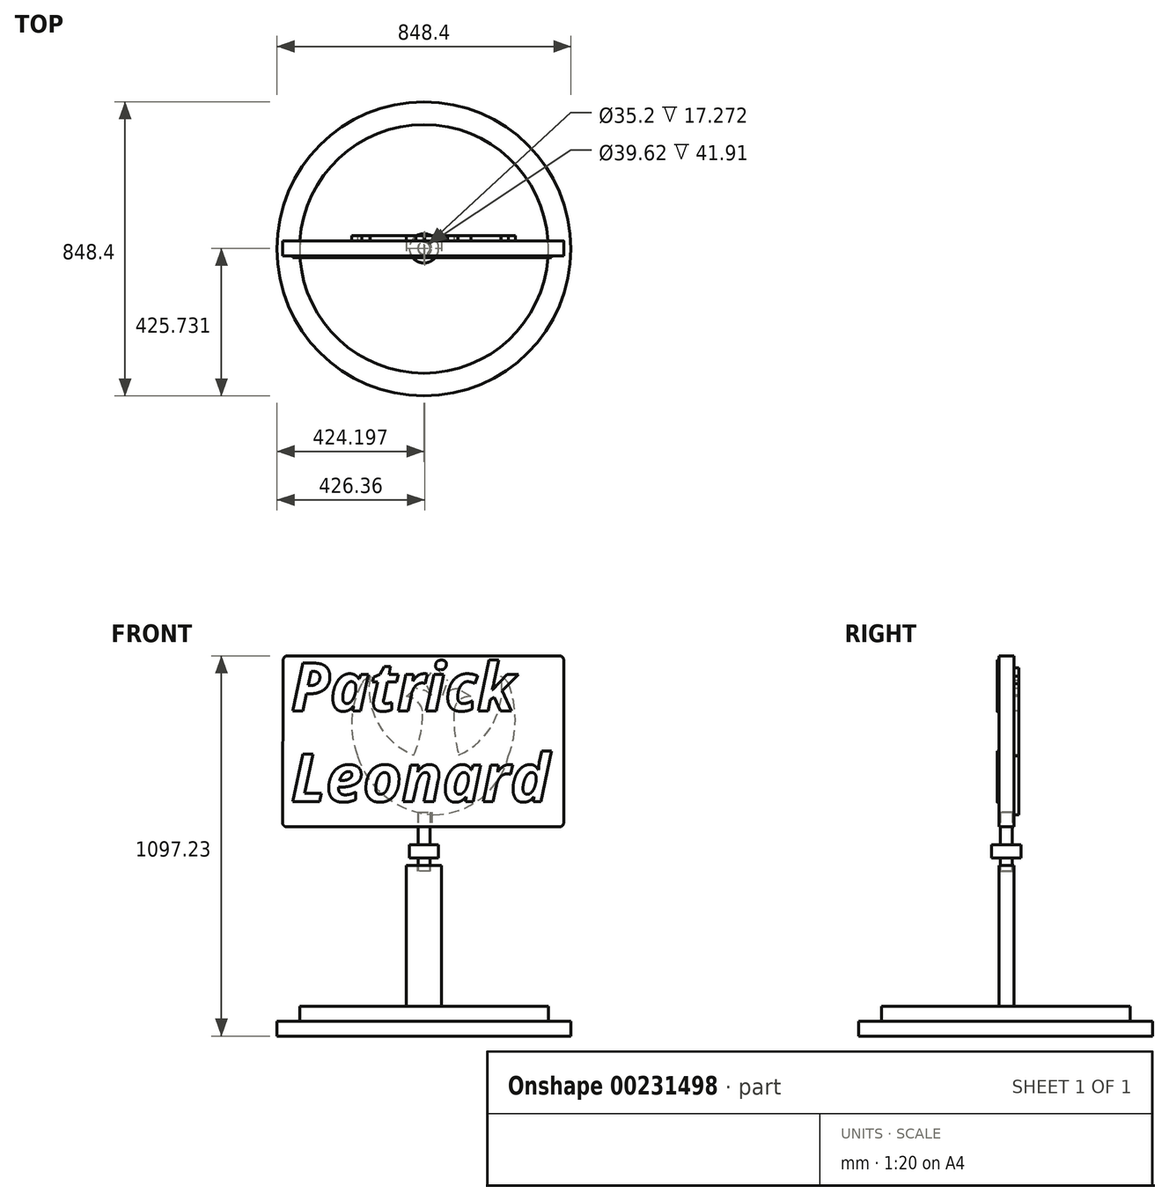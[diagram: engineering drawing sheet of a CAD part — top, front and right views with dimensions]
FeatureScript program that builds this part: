
annotation { "Feature Type Name" : "Feature", "Feature Type Description" : "" }
export const myFeature = defineFeature(function(context is Context, id is Id, definition is map)
    precondition{}
    {
        {
            var Q0;
            Q0=qCreatedBy(makeId("Front.planeOp"),FACE);
            var sketch = newSketch(context, id + "F0", { "sketchPlane" : qUnion([Q0])});
            skLineSegment(sketch, "E0", {"start": v(-180.52, -335) * mm, "end": v(631.48, -335) * mm});
            skLineSegment(sketch, "E1", {"start": v(631.48, -335) * mm, "end": v(631.48, 158.72) * mm});
            skLineSegment(sketch, "E2", {"start": v(631.48, 158.72) * mm, "end": v(-178.31, 158.72) * mm});
            skLineSegment(sketch, "E3", {"start": v(-178.31, 158.72) * mm, "end": v(-180.52, -335) * mm});
            skPoint(sketch, "E4.startSnap0", {"position": v(225.48, -335) * mm});
            skLineSegment(sketch, "E5", {"start": v(177.04, -445.85) * mm, "end": v(278.9, -445.85) * mm});
            skLineSegment(sketch, "E6", {"start": v(278.9, -445.85) * mm, "end": v(278.9, -852.15) * mm});
            skLineSegment(sketch, "E7", {"start": v(177.04, -445.85) * mm, "end": v(177.04, -852.15) * mm});
            skLineSegment(sketch, "E8", {"start": v(278.9, -852.15) * mm, "end": v(177.04, -852.15) * mm});
            skSolve(sketch);
        }
        {
            var Q0;
            Q0=makeQuery(id+"F0.imprint","IMPRINT",FACE,{"disambiguationData":[TD([[makeQuery(id+"F0.imprint","IMPRINT",EDGE,{"derivedFrom":sQuery(id+"F0.wireOp",EDGE,"E0")}),1.0]])]});
            var Q1;
            Q1=makeQuery(id+"F0.imprint","IMPRINT",FACE,{"disambiguationData":[TD([[makeQuery(id+"F0.imprint","IMPRINT",EDGE,{"derivedFrom":sQuery(id+"F0.wireOp",EDGE,"E5")}),-1.0]])]});
            extrude(context, id + "F1", {"entities" : qUnion([Q0, Q1]), "oppositeDirection" : true, "depth" : 43.32 * mm});
        }
        {
            var Q0;
            Q0=makeQuery(id+"F0.imprint","IMPRINT",FACE,{"disambiguationData":[TD([[makeQuery(id+"F0.imprint","IMPRINT",EDGE,{"derivedFrom":sQuery(id+"F0.wireOp",EDGE,"E0")}),1.0]])]});
            var sketch = newSketch(context, id + "F2", { "sketchPlane" : qUnion([Q0])});
            skText(sketch, "E9", { "text": "Patrick \nLeonard ", "fontName": "OpenSans-BoldItalic.ttf"});
            const initialGuessF2  = {"E9": [-0.15543, 0, 1, 0, 0.13875]};
            skSetInitialGuess(sketch, initialGuessF2);
            skSolve(sketch);
        }
        {
            var Q0;
            Q0 = qSketchRegion(id + "F2", true);
            extrude(context, id + "F3", {"entities" : qUnion([Q0]), "operationType" : NewBodyOperationType.ADD, "depth" : 5.08 * mm});
        }
        {
            var Q0;
            Q0=makeQuery(id+"F1.opExtrude","CAP_FACE",FACE,{"disambiguationData":[OSD([sQuery(id+"F0.wireOp",EDGE,"E0"),sQuery(id+"F0.wireOp",EDGE,"E1"),sQuery(id+"F0.wireOp",EDGE,"E2"),sQuery(id+"F0.wireOp",EDGE,"E3")])],"isStart":false});
            var sketch = newSketch(context, id + "F4", { "sketchPlane" : qUnion([Q0])});
            skArc(sketch, "E10", {"start": v(-471.9, -130.56) * mm, "mid": v(-392.37, -252.67) * mm, "end": v(-254.48, -299.8) * mm});
            skArc(sketch, "E11", {"start": v(-254.48, -299.8) * mm, "mid": v(-119.2, -248.99) * mm, "end": v(-36.4, -130.56) * mm});
            skArc(sketch, "E12", {"start": v(-36.4, -130.56) * mm, "mid": v(-19.4, -24.7) * mm, "end": v(-48.62, 78.48) * mm});
            skArc(sketch, "E13", {"start": v(-471.9, 78.48) * mm, "mid": v(-491.32, -26.04) * mm, "end": v(-471.9, -130.56) * mm});
            skArc(sketch, "E14", {"start": v(-449.7, 99.7) * mm, "mid": v(-462.17, 90.53) * mm, "end": v(-471.9, 78.48) * mm});
            skArc(sketch, "E15", {"start": v(-48.62, 78.48) * mm, "mid": v(-58.42, 91.44) * mm, "end": v(-72.42, 99.7) * mm});
            skArc(sketch, "E16", {"start": v(-198.5, -128.02) * mm, "mid": v(-95.23, -36.43) * mm, "end": v(-72.42, 99.7) * mm});
            skArc(sketch, "E17", {"start": v(-449.7, 99.7) * mm, "mid": v(-427.86, -34.81) * mm, "end": v(-328.45, -128.02) * mm});
            skArc(sketch, "E18", {"start": v(-328.45, -128.02) * mm, "mid": v(-316.4, -64.57) * mm, "end": v(-314.94, 0) * mm});
            skArc(sketch, "E19", {"start": v(-223.6, 0) * mm, "mid": v(-218.53, -65.48) * mm, "end": v(-198.5, -128.02) * mm});
            skArc(sketch, "E20", {"start": v(-177.27, 41.16) * mm, "mid": v(-207.43, 28.46) * mm, "end": v(-223.6, 0) * mm});
            skArc(sketch, "E21", {"start": v(-314.94, 0) * mm, "mid": v(-330.45, 30.67) * mm, "end": v(-363.18, 41.16) * mm});
            skLineSegment(sketch, "E22", {"start": v(-177.27, 41.16) * mm, "end": v(-204.93, 63.92) * mm});
            skLineSegment(sketch, "E23", {"start": v(-363.18, 41.16) * mm, "end": v(-325.23, 63.92) * mm});
            skArc(sketch, "E24", {"start": v(-204.93, 63.92) * mm, "mid": v(-229.31, 58.65) * mm, "end": v(-250.6, 45.67) * mm});
            skLineSegment(sketch, "E25", {"start": v(-250.6, 45.67) * mm, "end": v(-230.02, 86.84) * mm});
            skLineSegment(sketch, "E26", {"start": v(-230.02, 86.84) * mm, "end": v(-262.83, 124.15) * mm});
            skLineSegment(sketch, "E27", {"start": v(-262.83, 124.15) * mm, "end": v(-296.28, 86.84) * mm});
            skArc(sketch, "E28", {"start": v(-282.77, 45.67) * mm, "mid": v(-302.5, 58.3) * mm, "end": v(-325.23, 63.92) * mm});
            skLineSegment(sketch, "E29", {"start": v(-282.77, 45.67) * mm, "end": v(-296.28, 86.84) * mm});
            skSolve(sketch);
        }
        {
            var Q0;
            Q0=makeQuery(id+"F4.imprint","IMPRINT",FACE,{"disambiguationData":[TD([[makeQuery(id+"F4.imprint","IMPRINT",EDGE,{"derivedFrom":sQuery(id+"F4.wireOp",EDGE,"E10")}),1.0]])]});
            extrude(context, id + "F5", {"entities" : qUnion([Q0]), "operationType" : NewBodyOperationType.ADD, "depth" : 14.48 * mm});
        }
        {
            var Q0;
            Q0=makeQuery(id+"F1.opExtrude","SWEPT_FACE",FACE,{"disambiguationData":[OSD([sQuery(id+"F0.wireOp",EDGE,"E8")])]});
            var sketch = newSketch(context, id + "F6", { "sketchPlane" : qUnion([Q0])});
            skCircle(sketch, "E30", {"center": v(227.97, -20.13) * mm, "radius": 358.87 * mm});
            skPoint(sketch, "E30.centerSnap0", {"position": v(227.97, 0) * mm});
            skSolve(sketch);
        }
        {
            var Q0;
            Q0=makeQuery(id+"F6.imprint","IMPRINT",FACE,{"disambiguationData":[TD([[makeQuery(id+"F6.imprint","IMPRINT",EDGE,{"derivedFrom":sQuery(id+"F6.wireOp",EDGE,"E30")}),1.0]])]});
            var Q1;
            {var subQ0=sQuery(id+"F0.wireOp",EDGE,"E8");Q1=makeQuery(id+"F6.imprint","IMPRINT",FACE,{"disambiguationData":[TD([[makeQuery(id+"F6.imprint","IMPRINT",EDGE,{"derivedFrom":makeQuery(id+"F1.opExtrude","CAP_EDGE",EDGE,{"disambiguationData":[OSD([subQ0])],"isStart":true})}),1.0]])]});}
            extrude(context, id + "F7", {"entities" : qUnion([Q0, Q1]), "operationType" : NewBodyOperationType.ADD, "depth" : 43.18 * mm});
        }
        {
            var Q0;
            Q0=makeQuery(id+"F7.opExtrude","CAP_FACE",FACE,{"disambiguationData":[OSD([sQuery(id+"F6.wireOp",EDGE,"E30")])],"isStart":false});
            var sketch = newSketch(context, id + "F8", { "sketchPlane" : qUnion([Q0])});
            skCircle(sketch, "E31", {"center": v(227.97, -20.13) * mm, "radius": 424.2 * mm});
            skSolve(sketch);
        }
        {
            var Q0;
            Q0=makeQuery(id+"F8.imprint","IMPRINT",FACE,{"disambiguationData":[TD([[makeQuery(id+"F8.imprint","IMPRINT",EDGE,{"derivedFrom":sQuery(id+"F8.wireOp",EDGE,"E31")}),1.0]])]});
            var Q1;
            Q1=makeQuery(id+"F8.imprint","IMPRINT",FACE,{"disambiguationData":[TD([[makeQuery(id+"F8.imprint","IMPRINT",EDGE,{"derivedFrom":makeQuery(id+"F7.opExtrude","CAP_EDGE",EDGE,{"disambiguationData":[OSD([sQuery(id+"F6.wireOp",EDGE,"E30")])],"isStart":false})}),1.0]])]});
            extrude(context, id + "F9", {"entities" : qUnion([Q0, Q1]), "operationType" : NewBodyOperationType.ADD, "depth" : 43.18 * mm});
        }
        {
            var Q0;
            Q0=makeQuery(id+"F1.opExtrude","SWEPT_EDGE",EDGE,{"disambiguationData":[OSD([sQuery(id+"F0.wireOp",EDGE,"E1"),sQuery(id+"F0.wireOp",EDGE,"E2")])]});
            var Q1;
            Q1=makeQuery(id+"F1.opExtrude","SWEPT_EDGE",EDGE,{"disambiguationData":[OSD([sQuery(id+"F0.wireOp",EDGE,"E0"),sQuery(id+"F0.wireOp",EDGE,"E1")])]});
            var Q2;
            Q2=makeQuery(id+"F1.opExtrude","SWEPT_EDGE",EDGE,{"disambiguationData":[OSD([sQuery(id+"F0.wireOp",EDGE,"E0"),sQuery(id+"F0.wireOp",EDGE,"E3")])]});
            var Q3;
            Q3=makeQuery(id+"F1.opExtrude","SWEPT_EDGE",EDGE,{"disambiguationData":[OSD([sQuery(id+"F0.wireOp",EDGE,"E2"),sQuery(id+"F0.wireOp",EDGE,"E3")])]});
            fillet(context, id + "F10", {"entities" : qUnion([Q0, Q1, Q2, Q3]), "radius" : 12.7 * mm, "tangentPropagation" : true, "allowEdgeOverflow" : false});
        }
        {
            var Q0;
            Q0=makeQuery(id+"F1.opExtrude","SWEPT_FACE",FACE,{"disambiguationData":[OSD([sQuery(id+"F0.wireOp",EDGE,"E5")])]});
            var sketch = newSketch(context, id + "F11", { "sketchPlane" : qUnion([Q0])});
            skCircle(sketch, "E32", {"center": v(227.97, 21.66) * mm, "radius": 17.6 * mm});
            skPoint(sketch, "E32.centerSnap0", {"position": v(177.04, 21.66) * mm});
            skPoint(sketch, "E32.centerSnap1", {"position": v(227.97, 43.32) * mm});
            skSolve(sketch);
        }
        {
            var Q0;
            Q0=makeQuery(id+"F11.imprint","IMPRINT",FACE,{"disambiguationData":[TD([[makeQuery(id+"F11.imprint","IMPRINT",EDGE,{"derivedFrom":sQuery(id+"F11.wireOp",EDGE,"E32")}),1.0]])]});
            extrude(context, id + "F12", {"entities" : qUnion([Q0]), "operationType" : NewBodyOperationType.REMOVE, "oppositeDirection" : true, "depth" : 17.27 * mm});
        }
        {
            var Q0;
            Q0=makeQuery(id+"F12.boolean.opBoolean","COPY",FACE,{"derivedFrom":makeQuery(id+"F12.opExtrude","CAP_FACE",FACE,{"disambiguationData":[OSD([sQuery(id+"F11.wireOp",EDGE,"E32")])],"isStart":false})});
            var sketch = newSketch(context, id + "F13", { "sketchPlane" : qUnion([Q0])});
            skCircle(sketch, "E33", {"center": v(227.97, 21.66) * mm, "radius": 17.25 * mm});
            skSolve(sketch);
        }
        {
            var Q0;
            Q0=makeQuery(id+"F13.imprint","IMPRINT",FACE,{"disambiguationData":[TD([[makeQuery(id+"F13.imprint","IMPRINT",EDGE,{"derivedFrom":sQuery(id+"F13.wireOp",EDGE,"E33")}),1.0]])]});
            extrude(context, id + "F14", {"entities" : qUnion([Q0]), "operationType" : NewBodyOperationType.ADD, "depth" : 57.15 * mm});
        }
        {
            var Q0;
            Q0=makeQuery(id+"F14.opExtrude","CAP_FACE",FACE,{"disambiguationData":[OSD([sQuery(id+"F13.wireOp",EDGE,"E33")])],"isStart":false});
            var sketch = newSketch(context, id + "F15", { "sketchPlane" : qUnion([Q0])});
            skCircle(sketch, "E34", {"center": v(227.97, 21.66) * mm, "radius": 42.07 * mm});
            skSolve(sketch);
        }
        {
            var Q0;
            Q0=makeQuery(id+"F15.imprint","IMPRINT",FACE,{"disambiguationData":[TD([[makeQuery(id+"F15.imprint","IMPRINT",EDGE,{"derivedFrom":sQuery(id+"F15.wireOp",EDGE,"E34")}),1.0]])]});
            extrude(context, id + "F16", {"entities" : qUnion([Q0]), "operationType" : NewBodyOperationType.ADD, "endBound" : BoundingType.SYMMETRIC, "depth" : 37.8 * mm});
        }
        {
            var Q0;
            Q0=makeQuery(id+"F14.opExtrude","CAP_FACE",FACE,{"disambiguationData":[OSD([sQuery(id+"F13.wireOp",EDGE,"E33")])],"isStart":false});
            var sketch = newSketch(context, id + "F17", { "sketchPlane" : qUnion([Q0])});
            skCircle(sketch, "E35", {"center": v(227.97, 21.66) * mm, "radius": 17.3 * mm});
            skSolve(sketch);
        }
        {
            var Q0;
            Q0 = qSketchRegion(id + "F17", true);
            extrude(context, id + "F18", {"entities" : qUnion([Q0]), "operationType" : NewBodyOperationType.ADD, "depth" : 111.76 * mm});
        }
        {
            var Q0;
            Q0=makeQuery(id+"F1.opExtrude","SWEPT_FACE",FACE,{"disambiguationData":[OSD([sQuery(id+"F0.wireOp",EDGE,"E0")])]});
            var sketch = newSketch(context, id + "F19", { "sketchPlane" : qUnion([Q0])});
            skCircle(sketch, "E36", {"center": v(230.13, -21.66) * mm, "radius": 19.81 * mm});
            skPoint(sketch, "E36.centerSnap0", {"position": v(618.78, -21.66) * mm});
            skSolve(sketch);
        }
        {
            var Q0;
            Q0=makeQuery(id+"F19.imprint","IMPRINT",FACE,{"disambiguationData":[TD([[makeQuery(id+"F19.imprint","IMPRINT",EDGE,{"derivedFrom":sQuery(id+"F19.wireOp",EDGE,"E36")}),1.0]])]});
            extrude(context, id + "F20", {"entities" : qUnion([Q0]), "operationType" : NewBodyOperationType.REMOVE, "oppositeDirection" : true, "depth" : 41.9 * mm});
        }
    });
